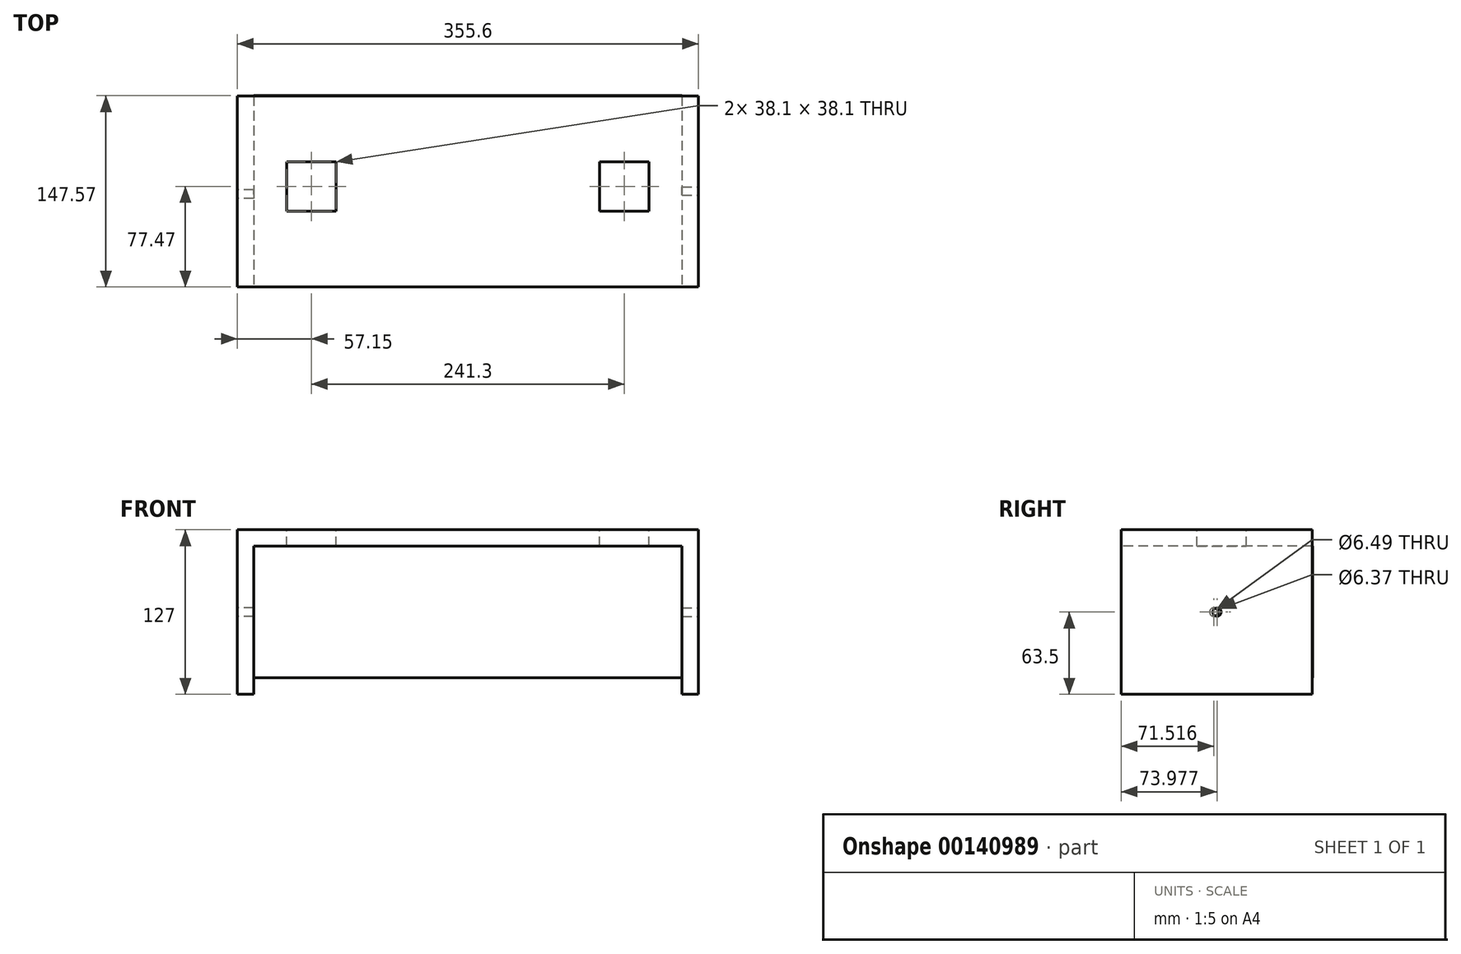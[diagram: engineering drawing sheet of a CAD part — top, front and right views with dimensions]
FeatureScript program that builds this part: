
annotation { "Feature Type Name" : "Feature", "Feature Type Description" : "" }
export const myFeature = defineFeature(function(context is Context, id is Id, definition is map)
    precondition{}
    {
        {
            var Q0;
            Q0=qCreatedBy(makeId("Front.planeOp"),FACE);
            var sketch = newSketch(context, id + "F0", { "sketchPlane" : qUnion([Q0])});
            skLineSegment(sketch, "E0.bottom", {"start": v(177.8, -63.5) * mm, "end": v(-177.8, -63.5) * mm});
            skLineSegment(sketch, "E0.top", {"start": v(177.8, 63.5) * mm, "end": v(-177.8, 63.5) * mm});
            skLineSegment(sketch, "E0.left", {"start": v(177.8, -63.5) * mm, "end": v(177.8, 63.5) * mm});
            skLineSegment(sketch, "E0.right", {"start": v(-177.8, -63.5) * mm, "end": v(-177.8, 63.5) * mm});
            skPoint(sketch, "E0.middle", {"position": v(0, 0) * mm});
            skSolve(sketch);
        }
        {
            var Q0;
            Q0=qSketchRegion(id+"F0",true);
            extrude(context, id + "F1", {"entities" : qUnion([Q0]), "depth" : 147.32 * mm});
        }
        {
            var Q0;
            Q0=makeQuery(id+"F1.opExtrude","CAP_FACE",FACE,{"disambiguationData":[OSD([sQuery(id+"F0.wireOp",EDGE,"E0.bottom"),sQuery(id+"F0.wireOp",EDGE,"E0.top"),sQuery(id+"F0.wireOp",EDGE,"E0.left"),sQuery(id+"F0.wireOp",EDGE,"E0.right")])],"isStart":false});
            var sketch = newSketch(context, id + "F2", { "sketchPlane" : qUnion([Q0])});
            skLineSegment(sketch, "E1.bottom", {"start": v(165.1, -50.8) * mm, "end": v(-165.1, -50.8) * mm});
            skLineSegment(sketch, "E1.top", {"start": v(165.1, 50.8) * mm, "end": v(-165.1, 50.8) * mm});
            skLineSegment(sketch, "E1.left", {"start": v(165.1, -50.8) * mm, "end": v(165.1, 50.8) * mm});
            skLineSegment(sketch, "E1.right", {"start": v(-165.1, -50.8) * mm, "end": v(-165.1, 50.8) * mm});
            skPoint(sketch, "E1.middle", {"position": v(0, 0) * mm});
            skSolve(sketch);
        }
        {
            var Q0;
            Q0=qSketchRegion(id+"F2",true);
            extrude(context, id + "F3", {"entities" : qUnion([Q0]), "operationType" : NewBodyOperationType.REMOVE, "endBound" : BoundingType.UP_TO_NEXT, "oppositeDirection" : true, "depth" : 25.4 * mm});
        }
        {
            var Q0;
            Q0=makeQuery(id+"F1.opExtrude","CAP_FACE",FACE,{"disambiguationData":[OSD([sQuery(id+"F0.wireOp",EDGE,"E0.bottom"),sQuery(id+"F0.wireOp",EDGE,"E0.top"),sQuery(id+"F0.wireOp",EDGE,"E0.left"),sQuery(id+"F0.wireOp",EDGE,"E0.right")])],"isStart":true});
            var sketch = newSketch(context, id + "F4", { "sketchPlane" : qUnion([Q0])});
            skLineSegment(sketch, "E2.bottom", {"start": v(-165.1, 50.8) * mm, "end": v(165.1, 50.8) * mm});
            skLineSegment(sketch, "E2.top", {"start": v(-165.1, -50.8) * mm, "end": v(165.1, -50.8) * mm});
            skLineSegment(sketch, "E2.left", {"start": v(-165.1, 50.8) * mm, "end": v(-165.1, -50.8) * mm});
            skLineSegment(sketch, "E2.right", {"start": v(165.1, 50.8) * mm, "end": v(165.1, -50.8) * mm});
            skSolve(sketch);
        }
        {
            var Q0;
            Q0=makeQuery(id+"F4.imprint","IMPRINT",FACE,{"disambiguationData":[TD([[makeQuery(id+"F4.imprint","IMPRINT",EDGE,{"derivedFrom":sQuery(id+"F4.wireOp",EDGE,"E2.bottom")}),1.0]])]});
            var sketch = newSketch(context, id + "F5", { "sketchPlane" : qUnion([Q0])});
            skLineSegment(sketch, "E3.bottom", {"start": v(-165.16, 50.09) * mm, "end": v(164.2, 50.09) * mm});
            skLineSegment(sketch, "E3.top", {"start": v(-165.16, -50.21) * mm, "end": v(164.2, -50.21) * mm});
            skLineSegment(sketch, "E3.left", {"start": v(-165.16, 50.09) * mm, "end": v(-165.16, -50.21) * mm});
            skLineSegment(sketch, "E3.right", {"start": v(164.2, 50.09) * mm, "end": v(164.2, -50.21) * mm});
            skSolve(sketch);
        }
        {
            var Q0;
            Q0=makeQuery(id+"F4.imprint","IMPRINT",FACE,{"disambiguationData":[TD([[makeQuery(id+"F4.imprint","IMPRINT",EDGE,{"derivedFrom":sQuery(id+"F4.wireOp",EDGE,"E2.bottom")}),1.0]])]});
            extrude(context, id + "F6", {"entities" : qUnion([Q0]), "depth" : 0.25 * mm});
        }
        {
            var Q0;
            Q0=makeQuery(id+"F1.opExtrude","SWEPT_FACE",FACE,{"disambiguationData":[OSD([sQuery(id+"F0.wireOp",EDGE,"E0.right")])]});
            var sketch = newSketch(context, id + "F7", { "sketchPlane" : qUnion([Q0])});
            skCircle(sketch, "E4", {"center": v(75.8, 0) * mm, "radius": 3.25 * mm});
            skSolve(sketch);
        }
        {
            var Q0;
            Q0=qSketchRegion(id+"F7",true);
            extrude(context, id + "F8", {"entities" : qUnion([Q0]), "operationType" : NewBodyOperationType.REMOVE, "oppositeDirection" : true, "depth" : 25.4 * mm});
        }
        {
            var Q0;
            Q0=makeQuery(id+"F1.opExtrude","SWEPT_FACE",FACE,{"disambiguationData":[OSD([sQuery(id+"F0.wireOp",EDGE,"E0.left")])]});
            var sketch = newSketch(context, id + "F9", { "sketchPlane" : qUnion([Q0])});
            skCircle(sketch, "E5", {"center": v(-73.34, 0) * mm, "radius": 3.19 * mm});
            skSolve(sketch);
        }
        {
            var Q0;
            Q0=qSketchRegion(id+"F9",true);
            extrude(context, id + "F10", {"entities" : qUnion([Q0]), "operationType" : NewBodyOperationType.REMOVE, "oppositeDirection" : true, "depth" : 25.4 * mm});
        }
        {
            var Q0;
            Q0=makeQuery(id+"F3.boolean.opBoolean","COPY",FACE,{"derivedFrom":makeQuery(id+"F3.opExtrude","SWEPT_FACE",FACE,{"disambiguationData":[OSD([sQuery(id+"F2.wireOp",EDGE,"E1.bottom")])]})});
            extrude(context, id + "F11", {"entities" : qUnion([Q0]), "operationType" : NewBodyOperationType.REMOVE, "oppositeDirection" : true, "depth" : 25.4 * mm});
        }
        {
            var Q0;
            Q0=makeQuery(id+"F1.opExtrude","SWEPT_FACE",FACE,{"disambiguationData":[OSD([sQuery(id+"F0.wireOp",EDGE,"E0.top")])]});
            var sketch = newSketch(context, id + "F12", { "sketchPlane" : qUnion([Q0])});
            skLineSegment(sketch, "E6.bottom", {"start": v(139.7, -88.9) * mm, "end": v(101.6, -88.9) * mm});
            skLineSegment(sketch, "E6.top", {"start": v(139.7, -50.8) * mm, "end": v(101.6, -50.8) * mm});
            skLineSegment(sketch, "E6.left", {"start": v(139.7, -88.9) * mm, "end": v(139.7, -50.8) * mm});
            skLineSegment(sketch, "E6.right", {"start": v(101.6, -88.9) * mm, "end": v(101.6, -50.8) * mm});
            skLineSegment(sketch, "E7.bottom", {"start": v(-101.6, -88.9) * mm, "end": v(-139.7, -88.9) * mm});
            skLineSegment(sketch, "E7.top", {"start": v(-101.6, -50.8) * mm, "end": v(-139.7, -50.8) * mm});
            skLineSegment(sketch, "E7.left", {"start": v(-101.6, -88.9) * mm, "end": v(-101.6, -50.8) * mm});
            skLineSegment(sketch, "E7.right", {"start": v(-139.7, -88.9) * mm, "end": v(-139.7, -50.8) * mm});
            skSolve(sketch);
        }
        {
            var Q0;
            Q0=makeQuery(id+"F12.imprint","IMPRINT",FACE,{"disambiguationData":[TD([[makeQuery(id+"F12.imprint","IMPRINT",EDGE,{"derivedFrom":sQuery(id+"F12.wireOp",EDGE,"E6.bottom")}),-1.0]])]});
            extrude(context, id + "F13", {"entities" : qUnion([Q0]), "operationType" : NewBodyOperationType.REMOVE, "oppositeDirection" : true, "depth" : 25.4 * mm});
        }
        {
            var Q0;
            Q0=makeQuery(id+"F12.imprint","IMPRINT",FACE,{"disambiguationData":[TD([[makeQuery(id+"F12.imprint","IMPRINT",EDGE,{"derivedFrom":sQuery(id+"F12.wireOp",EDGE,"E7.bottom")}),-1.0]])]});
            extrude(context, id + "F14", {"entities" : qUnion([Q0]), "operationType" : NewBodyOperationType.REMOVE, "oppositeDirection" : true, "depth" : 25.4 * mm});
        }
    });
